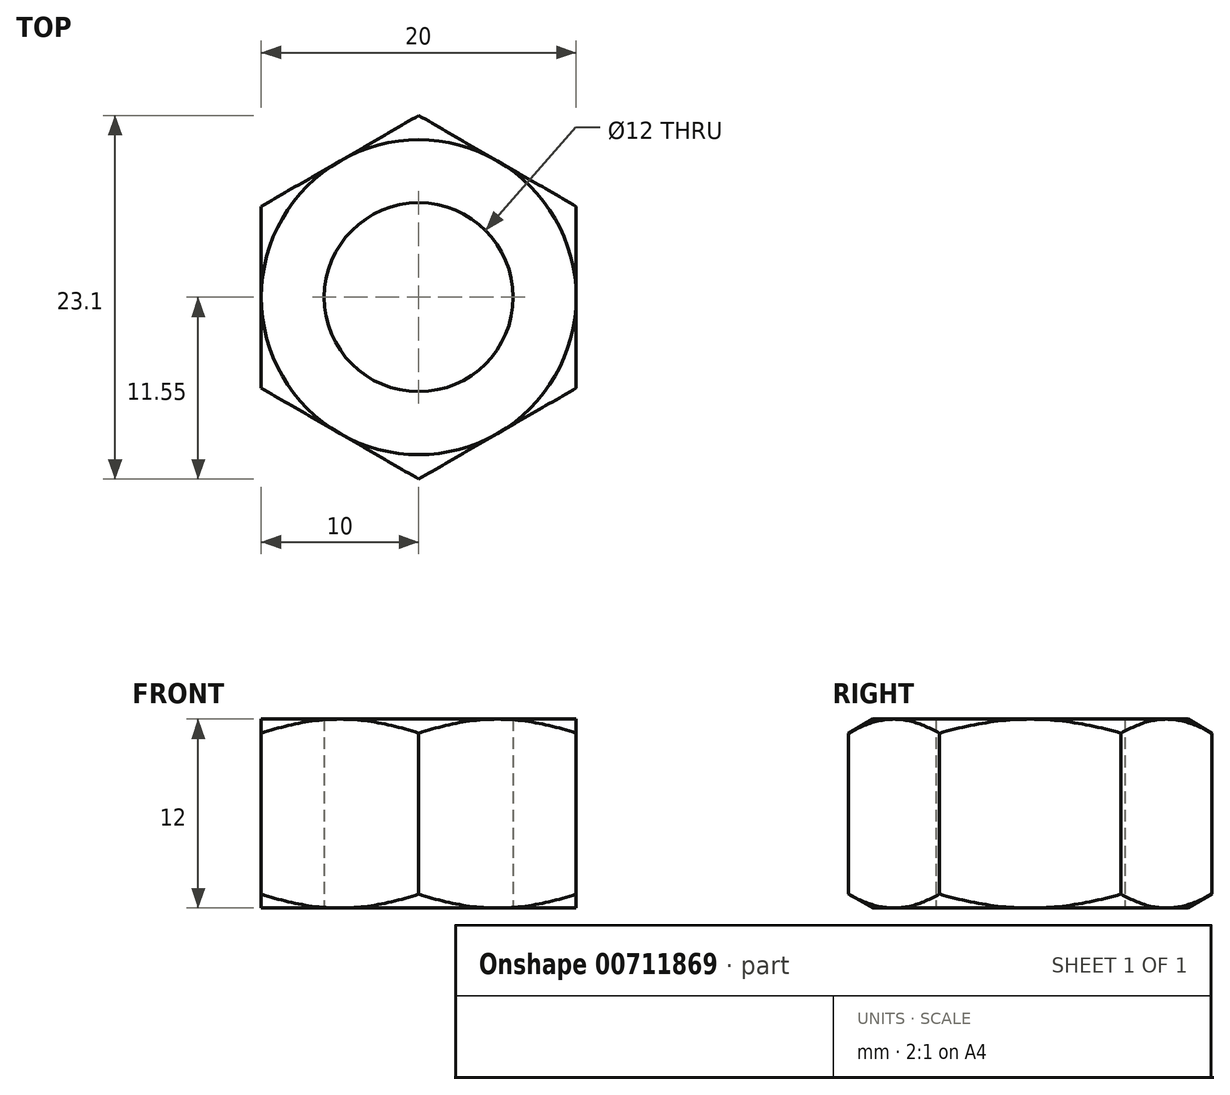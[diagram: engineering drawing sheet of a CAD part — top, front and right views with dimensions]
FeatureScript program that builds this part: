
annotation { "Feature Type Name" : "Feature", "Feature Type Description" : "" }
export const myFeature = defineFeature(function(context is Context, id is Id, definition is map)
    precondition{}
    {
        {
            var Q0;
            Q0=qCreatedBy(makeId("Top.planeOp"),FACE);
            var sketch = newSketch(context, id + "F0", { "sketchPlane" : qUnion([Q0])});
            skCircle(sketch, "E0.cCircle", {"center": v(0, 0) * mm, "radius": 10 * mm, "construction": true});
            skLineSegment(sketch, "E0.0", {"start": v(0, 11.55) * mm, "end": v(10, 5.77) * mm});
            skLineSegment(sketch, "E0.1", {"start": v(10, 5.77) * mm, "end": v(10, -5.77) * mm});
            skLineSegment(sketch, "E0.2", {"start": v(10, -5.77) * mm, "end": v(0, -11.55) * mm});
            skLineSegment(sketch, "E0.3", {"start": v(0, -11.55) * mm, "end": v(-10, -5.77) * mm});
            skLineSegment(sketch, "E0.4", {"start": v(-10, -5.77) * mm, "end": v(-10, 5.77) * mm});
            skLineSegment(sketch, "E0.5", {"start": v(-10, 5.77) * mm, "end": v(0, 11.55) * mm});
            skPoint(sketch, "E0.0.midPoint", {"position": v(5, 8.66) * mm});
            skCircle(sketch, "E1", {"center": v(0, 0) * mm, "radius": 6 * mm});
            skSolve(sketch);
        }
        {
            var Q0;
            Q0 = qSketchRegion(id + "F0", true);
            extrude(context, id + "F1", {"entities" : qUnion([Q0]), "depth" : 12 * mm, "offsetDistance" : 25 * mm});
        }
        {
            var Q0;
            Q0=qCreatedBy(makeId("Front.planeOp"),FACE);
            var sketch = newSketch(context, id + "F2", { "sketchPlane" : qUnion([Q0])});
            skLineSegment(sketch, "E2", {"start": v(0, 0) * mm, "end": v(0, 12) * mm, "construction": true});
            skLineSegment(sketch, "E3", {"start": v(0, 6) * mm, "end": v(8.22, 6) * mm, "construction": true});
            skLineSegment(sketch, "E4", {"start": v(10, 12) * mm, "end": v(14.07, 12) * mm});
            skLineSegment(sketch, "E5", {"start": v(14.07, 12) * mm, "end": v(14.07, 9.65) * mm});
            skLineSegment(sketch, "E6", {"start": v(14.07, 9.65) * mm, "end": v(10, 12) * mm});
            skLineSegment(sketch, "E7.MirrorCS", {"start": v(14.07, 2.35) * mm, "end": v(10, 0) * mm});
            skLineSegment(sketch, "E8.MirrorCS", {"start": v(10, 0) * mm, "end": v(14.07, 0) * mm});
            skLineSegment(sketch, "E9.MirrorCS", {"start": v(14.07, 0) * mm, "end": v(14.07, 2.35) * mm});
            skSolve(sketch);
        }
        {
            var Q0;
            Q0=makeQuery(id+"F2.imprint","IMPRINT",FACE,{"disambiguationData":[TD([[makeQuery(id+"F2.imprint","IMPRINT",EDGE,{"derivedFrom":sQuery(id+"F2.wireOp",EDGE,"E4")}),-1.0]])]});
            var Q1;
            Q1=makeQuery(id+"F2.imprint","IMPRINT",FACE,{"disambiguationData":[TD([[makeQuery(id+"F2.imprint","IMPRINT",EDGE,{"derivedFrom":sQuery(id+"F2.wireOp",EDGE,"E7.MirrorCS")}),1.0]])]});
            var Q2;
            Q2=sQuery(id+"F2.wireOp",EDGE,"E2");
            revolve(context, id + "F3", {"operationType" : NewBodyOperationType.REMOVE, "surfaceOperationType" : NewSurfaceOperationType.NEW, "entities" : qUnion([Q0, Q1]), "axis" : qUnion([Q2]), "revolveType" : RevolveType.FULL, "oppositeDirection" : true});
        }
    });
